# Revit family: Hager-Volta-IP30-syst-DE-de
name_source: partatom
category: Electrical Equipment
units: mm (PartAtom-declared; Revit-internal decimal feet)

## family parameters
Cut with Voids When Loaded = No
Host = Face
Panel Configuration = Two Columns, Circuits Across
Part Type = Panelboard
Room Calculation Point = No
Round Connector Dimension = Use Diameter
Shared = No

## types (4) — shared parameters
EF000003 - Montageart = EV000384 - Aufputz
EF000008 - Breite = 305 mm  [stored 1.00066 ft]
EF000049 - Tiefe = 97 mm  [stored 0.318241 ft]
EF000118 - Mit Montageplatte = No
EF001062 - EMV-Ausführung = No
EF001088 - Anbaumöglichkeit = No
EF001134 - DIN-Schiene = No
EF001596 - Werkstoff des Gehäuses = EV000139 - Kunststoff
EF002950 - Breite in Teilungseinheiten = 12
EF004462 - Art der Schließung = EV000154 - sonstige
EF005474 - Schutzart (IP) = EV006410 - IP30
EF006244 - Transparenter Deckel/Tür = Yes
EF006306 - Mit Schloss = No
EF015776 - Erdungsklemmenblock = No
EF015777 - Neutralleiterklemmenblock = No
EF015941 - Signaldurchlassende Tür = No
HG000001 - Anzahl der Spalten = 1
HG000002 - Mit tür = Yes
HG000003 - Bereich = Volta
HG000005 - Dicke = 3 mm  [stored 0.00984252 ft]
HG000006 - Unterputz = No
HG000009 - Doppelflügeligen Tür = No
HG000010 - Asymmetrische Türen = No
HG000011 - Leere Reihen von unten = No
HG000017 - Distanz zwischen den Polen = 18 mm  [stored 0.0590551 ft]
Manufacturer = Hager
Type Comments = Volta
zero-valued in all types: Default Elevation, EF000218 - Einbautiefe, EF000332 - Einbauhöhe, EF000846 - Einbaubreite, EF001131 - Innentiefe, HG000007 - Anzahl der leeren Spalten, HG000008 - Anzahl der leeren Reihen

## per-type parameters (varying)
| type | EF000040 - Höhe | EF000116 - RAL-Nummer | EF000266 - Anzahl der Reihen | HG000004 - Herstellerreferenz | Model |
| Aufputz IP30 B305 H245 T97 12 Teilungseinheiten - G44037035 | 245 mm | 7035 | 1 | G44037035 | G44037035 |
| Aufputz IP30 B305 H245 T97 12 Teilungseinheiten - G44039010 | 245 mm | 9010 | 1 | G44039010 | G44039010 |
| Aufputz IP30 B305 H370 T97 12 Teilungseinheiten - G44047035 | 370 mm  [stored 1.21391 ft] | 7035 | 2 | G44047035 | G44047035 |
| Aufputz IP30 B305 H370 T97 12 Teilungseinheiten - G44049010 | 370 mm  [stored 1.21391 ft] | 9010 | 2 | G44049010 | G44049010 |

note: [stored X ft] marks values corroborated as IEEE doubles in the binary element streams (Revit-internal decimal feet)

## geometry (parser evidence)
native form markers: Sweep x17
no freeform markers — native parametric forms only
